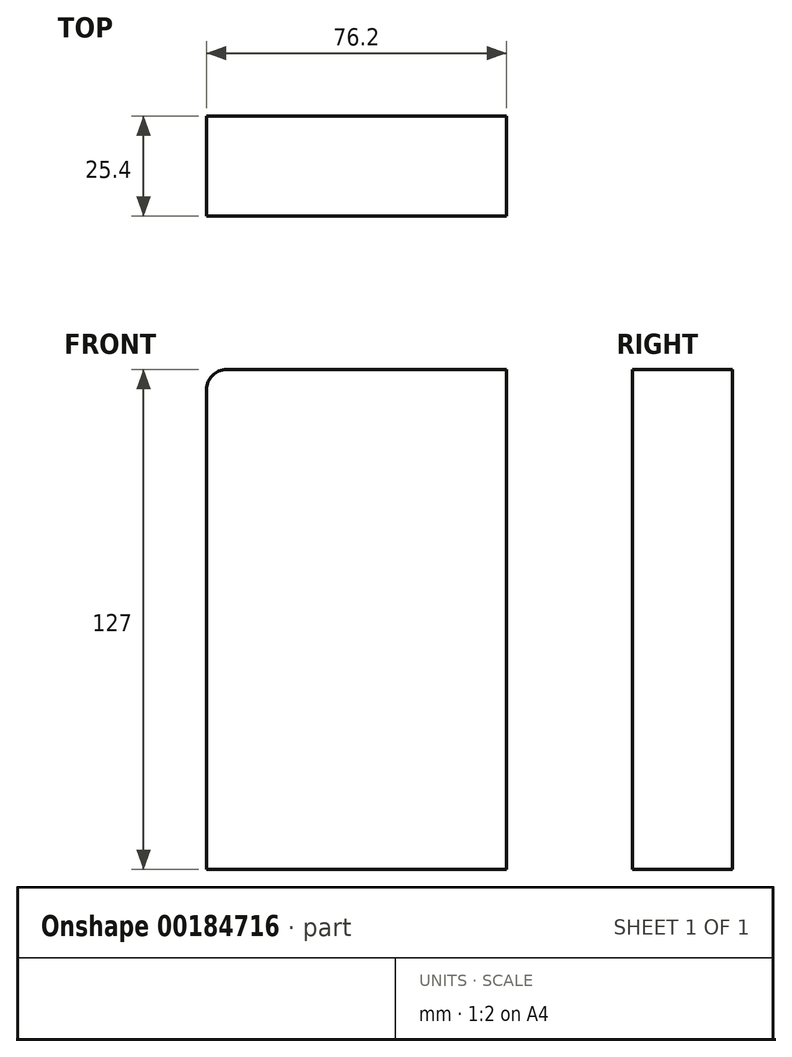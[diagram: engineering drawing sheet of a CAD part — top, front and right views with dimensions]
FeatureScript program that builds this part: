
annotation { "Feature Type Name" : "Feature", "Feature Type Description" : "" }
export const myFeature = defineFeature(function(context is Context, id is Id, definition is map)
    precondition{}
    {
        {
            var Q0;
            Q0=qCreatedBy(makeId("Front.planeOp"),FACE);
            var sketch = newSketch(context, id + "F0", { "sketchPlane" : qUnion([Q0])});
            skLineSegment(sketch, "E0.bottom", {"start": v(-76.2, 127) * mm, "end": v(0, 127) * mm});
            skLineSegment(sketch, "E0.top", {"start": v(-76.2, 0) * mm, "end": v(0, 0) * mm});
            skLineSegment(sketch, "E0.left", {"start": v(-76.2, 127) * mm, "end": v(-76.2, 0) * mm});
            skLineSegment(sketch, "E0.right", {"start": v(0, 127) * mm, "end": v(0, 0) * mm});
            skSolve(sketch);
        }
        {
            var Q0;
            Q0=makeQuery(id+"F0.imprint","IMPRINT",FACE,{"disambiguationData":[TD([[makeQuery(id+"F0.imprint","IMPRINT",EDGE,{"derivedFrom":sQuery(id+"F0.wireOp",EDGE,"E0.bottom")}),-1.0]])]});
            extrude(context, id + "F1", {"entities" : qUnion([Q0]), "depth" : 25.4 * mm});
        }
        {
            var Q0;
            Q0=makeQuery(id+"F1.opExtrude","SWEPT_EDGE",EDGE,{"disambiguationData":[OSD([sQuery(id+"F0.wireOp",EDGE,"E0.bottom"),sQuery(id+"F0.wireOp",EDGE,"E0.left")])]});
            fillet(context, id + "F2", {"entities" : qUnion([Q0]), "radius" : 5.08 * mm, "tangentPropagation" : true, "allowEdgeOverflow" : false});
        }
    });
